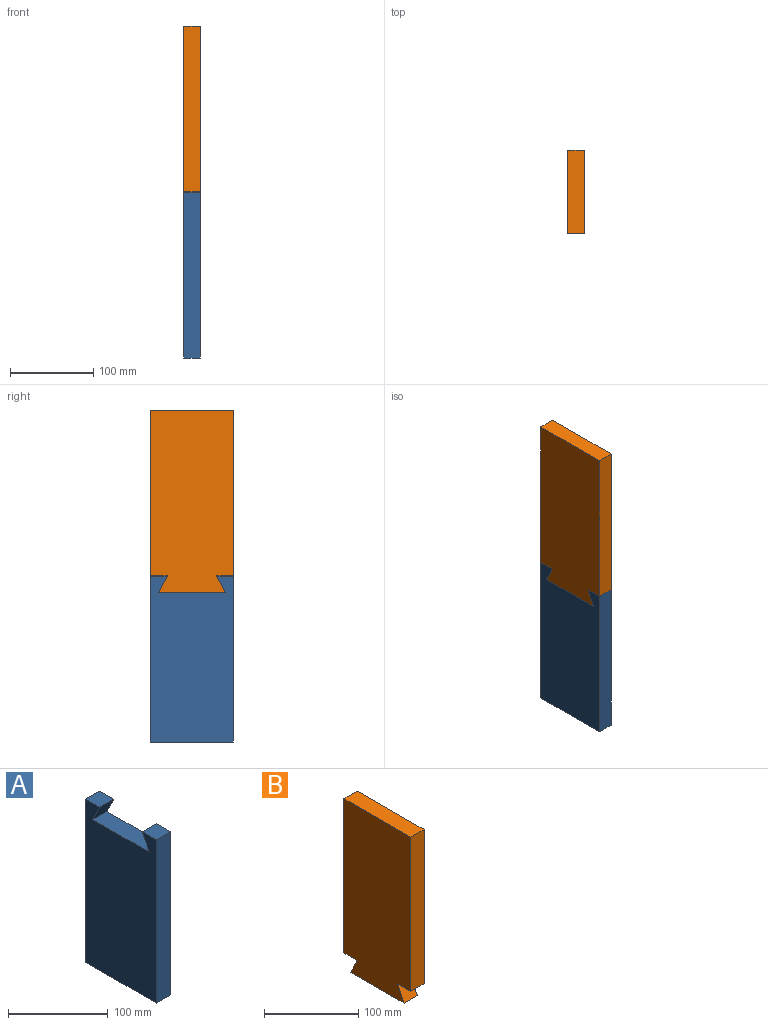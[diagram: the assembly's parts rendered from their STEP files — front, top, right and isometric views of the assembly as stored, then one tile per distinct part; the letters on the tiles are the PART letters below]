
ASSEMBLY  parts=2 mates=1
PART A: 10 faces, bbox 20x100x200 mm
  f0: plane 20x20mm, normal (0,0,1), area 400mm2, adj f1,f5,f6,f8
  f1: plane 200x100mm, normal (1,0,0), area 18600mm2, adj f0,f2,f3,f4,f5,f7,f8,f9
  f2: plane 20x20mm, normal (0,0,1), area 400mm2, adj f1,f3,f6,f9
  f3: plane 200x20mm, normal (0,-1,0), area 4000mm2, adj f1,f2,f4,f6
  f4: plane 100x20mm, normal (0,0,-1), area 2000mm2, adj f1,f3,f5,f6
  f5: plane 200x20mm, normal (0,1,0), area 4000mm2, adj f0,f1,f4,f6
  f6: plane 200x100mm, normal (-1,0,0), area 18600mm2, adj f0,f2,f3,f4,f5,f7,f8,f9
  f7: plane 80x20mm, normal (0,0,1), area 1600mm2, adj f1,f6,f8,f9
  f8: plane 20x20mm, normal (0,-0.89,-0.45), area 447.2mm2, adj f0,f1,f6,f7
  f9: plane 20x20mm, normal (0,0.89,-0.45), area 447.2mm2, adj f1,f2,f6,f7
PART B: 10 faces, bbox 20x100x220 mm
  f0: plane 20x20mm, normal (0,0,-1), area 400mm2, adj f1,f7,f8,f9
  f1: plane 20x20mm, normal (0,-0.89,0.45), area 447.2mm2, adj f0,f2,f8,f9
  f2: plane 80x20mm, normal (0,0,-1), area 1600mm2, adj f1,f3,f8,f9
  f3: plane 20x20mm, normal (0,0.89,0.45), area 447.2mm2, adj f2,f4,f8,f9
  f4: plane 20x20mm, normal (0,0,-1), area 400mm2, adj f3,f5,f8,f9
  f5: plane 200x20mm, normal (0,1,0), area 4000mm2, adj f4,f6,f8,f9
  f6: plane 100x20mm, normal (0,0,1), area 2000mm2, adj f5,f7,f8,f9
  f7: plane 200x20mm, normal (0,-1,0), area 4000mm2, adj f0,f6,f8,f9
  f8: plane 220x100mm, normal (1,0,0), area 21400mm2, adj f0,f1,f2,f3,f4,f5,f6,f7
  f9: plane 220x100mm, normal (-1,0,0), area 21400mm2, adj f0,f1,f2,f3,f4,f5,f6,f7
PLACE A t=(88.76,72.69,-191.58)mm
PLACE B t=(88.76,65.38,12.92)mm
MATE fastened A.f7 <-> B.f2  axis (0,0,1) through (98.76,59.07,-106.93)mm
